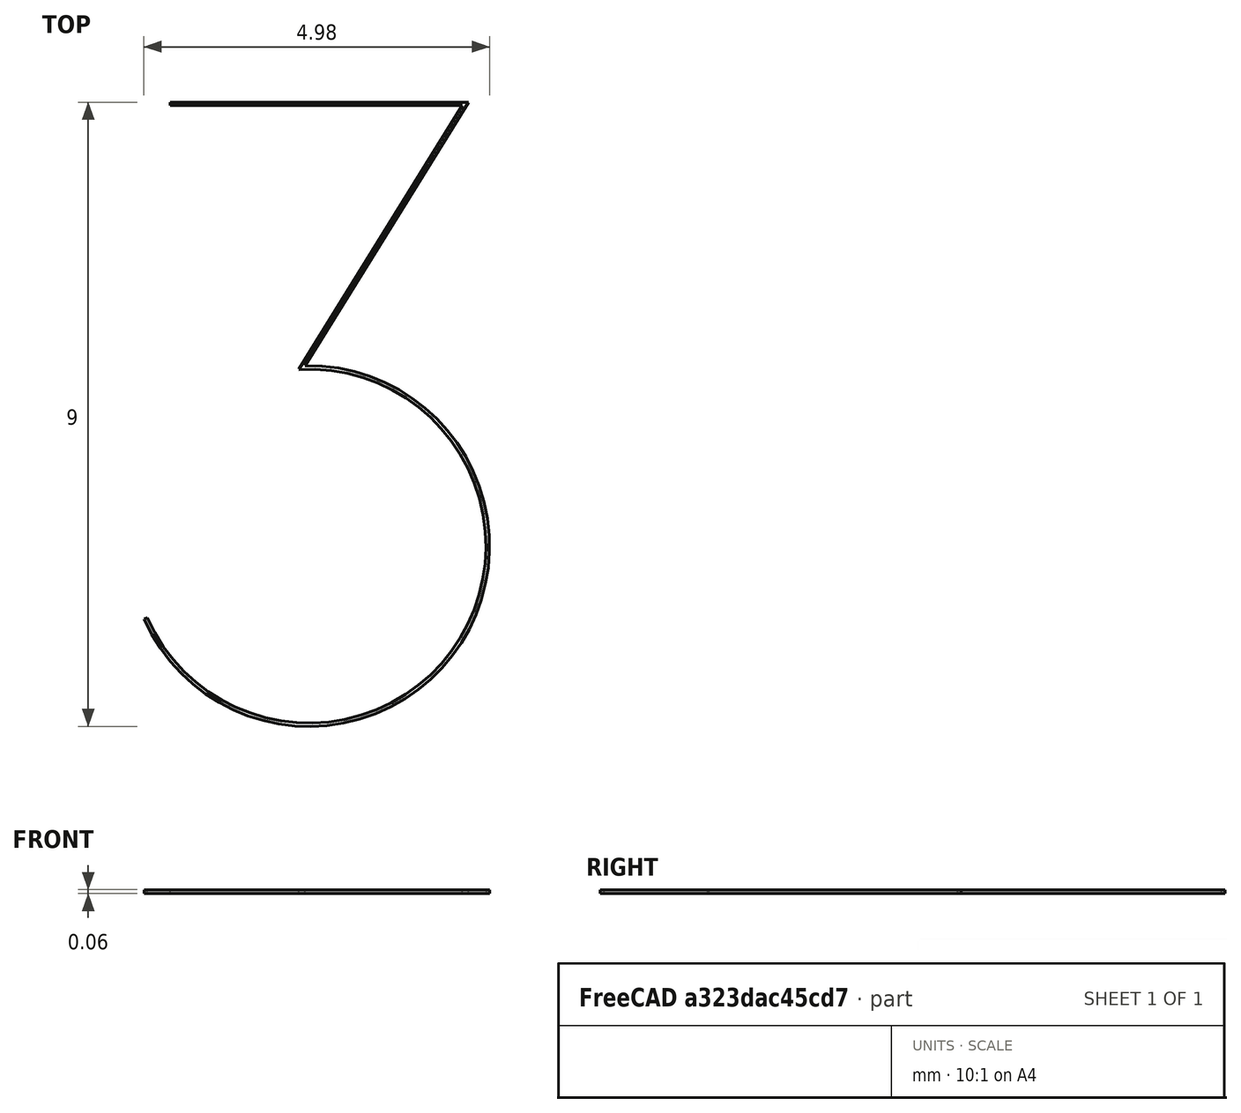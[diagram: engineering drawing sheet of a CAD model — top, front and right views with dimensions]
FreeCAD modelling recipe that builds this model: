
FCSTD DOCUMENT  (FreeCAD 0.16R6712 (Git))
Label: 3t
License: All rights reserved
LicenseURL: http://en.wikipedia.org/wiki/All_rights_reserved
objects: Sketcher::SketchObject×1, PartDesign::Pad×1, Mesh::Feature×1
note: 3 computed .brp shape members not serialized (recipe doc carries the construction recipe); baked Part::Feature solids carry a one-line shape summary decoded from their .brp

FEATURE [Sketcher::SketchObject] Sketch
  sketch-geometry (8):
    g0: ArcOfCircle CenterX=0 CenterY=2.6 CenterZ=0 NormalX=0 NormalY=0 NormalZ=1 Radius=2.55 StartAngle=3.55924 EndAngle=7.91232
    g1: LineSegment StartX=-2.33082 StartY=1.5657 StartZ=0 EndX=-2.37652 EndY=1.54542 EndZ=0
    g2: ArcOfCircle CenterX=0 CenterY=2.6 CenterZ=0 NormalX=0 NormalY=0 NormalZ=1 Radius=2.6 StartAngle=3.55924 EndAngle=7.87573
    g3: LineSegment StartX=-2 StartY=9 StartZ=0 EndX=2.3 EndY=9 EndZ=0
    g4: LineSegment StartX=-2 StartY=9 StartZ=0 EndX=-2 EndY=8.95 EndZ=0
    g5: LineSegment StartX=-2 StartY=8.95 StartZ=0 EndX=2.21017 EndY=8.95 EndZ=0
    g6: LineSegment StartX=2.21017 StartY=8.95 StartZ=0 EndX=-0.14869 EndY=5.14566 EndZ=0
    g7: LineSegment StartX=2.3 StartY=9 StartZ=0 EndX=-0.0565471 EndY=5.19939 EndZ=0
  constraints (23):
    c: Coincident(g1,g0)
    c: Perpendicular(g0,g1)
    c: Distance(g0,g1) = 0.05
    c: PointOnObject(g0,g-2)
    c: Coincident(g2,g0)
    c: Coincident(g2,g1)
    c: Tangent(g-1,g2)
    c: Horizontal(g3)
    c: Coincident(g4,g3)
    c: Vertical(g4)
    c: Horizontal(g5)
    c: Distance(g4,g3) = 0.05
    c: DistanceY(g-1,g3) = 9
    c: Coincident(g5,g4)
    c: Coincident(g6,g5)
    c: DistanceX(g-2,g3) = -2
    c: DistanceX(g-2,g3) = 2.3
    c: Coincident(g7,g3)
    c: Coincident(g2,g7)
    c: Coincident(g0,g6)
    c: Distance(g2,g6) = 0.05
    c: Radius(g2) = 2.6
    c: Parallel(g6,g7)
FEATURE [PartDesign::Pad] Pad
  Length = 0.05
  Length2 = 100
  Midplane = true
  Sketch = -> Sketch
  Type = 0
FEATURE [Mesh::Feature] Mesh  label="Pad (Meshed)"
